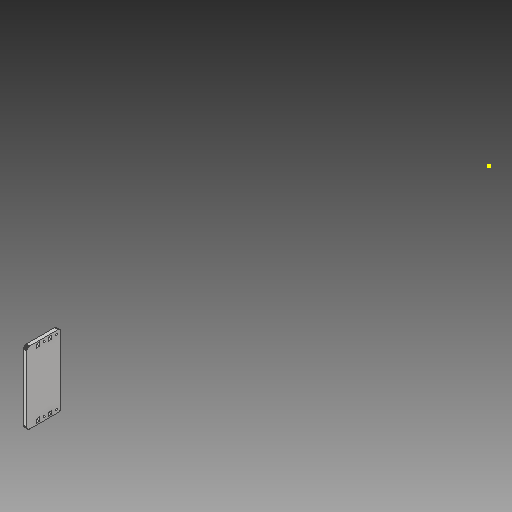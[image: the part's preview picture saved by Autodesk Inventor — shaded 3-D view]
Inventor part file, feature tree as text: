
AUTODESK INVENTOR PART (.ipt)
format: ipt  version: 2018 (Build 220112000, 112)  size: 357,376 bytes
history: native  units: mm
features: sketch x3, other x3, extrude x1, hole x1, reference x1
ambient origin geometry x8: Origin, YZ Plane, XZ Plane, XY Plane, X Axis, Y Axis, Z Axis, Center Point
bodies: Solid1 (feature_tree)
feature tree (9):
  extrude  "Extrusion1"  [1 undecoded]
  hole  "Hole1"  [1 undecoded]
  sketch  "Sketch3"
  sketch  "Sketch1"  dims[d0=6.0mm d1=0.0mm]
  sketch  "Sketch2"  dims[d2=3.2mm d3=6.0mm d4=4.0mm d5=2.0mm d6=90.0deg d7=8.0mm d8=20.594885mm]
  reference  "Reference1"
  parser-record x1  (decoder bookkeeping rows leaked as tree rows — omitted from the tree; the rows remain in map.json)
  other  "Assembly33.iam"
  other  "X Axis Brace_MIR:1"
note: 2 required parameter values undecoded (feature->parameter linkage not recoverable at this tier; creation-order binding heuristic only, values carry confidence <= 0.55)
note: 1 file-system path scrubbed to <path> (originals preserved in map.json)
